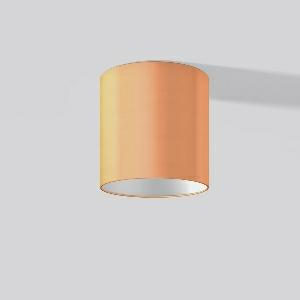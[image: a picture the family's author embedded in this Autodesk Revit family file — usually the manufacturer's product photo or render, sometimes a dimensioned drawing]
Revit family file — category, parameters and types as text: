
# Revit family: toledo_flatliner_901634_002_1_be23
name_source: partatom
category: Lighting Fixtures
units: mm (PartAtom-declared; Revit-internal decimal feet)

## family parameters
Cut with Voids When Loaded = No
Host = Face
Light Source = No
Part Type = Normal
Room Calculation Point = No
Round Connector Dimension = Use Diameter
Shared = No

## types (1)
- 982302.002 (1 x LED Modul 840, 1950 lm, 4000)
    Apparent Load = 22 VA
    CIE Flux Codes = 50 82 97 99 100
    Color Rendering = 80
    Color Temperature = 4000
    Default Elevation = 1800 mm
    Description = Series: TOLEDO FLATLINER
Decorative ceiling luminaire for interior decoration. Base luminaire prepared for the installation of fabric lampshade. Cylinder housing sheet steel, powder-coated. Housing: die cast aluminium and sheet steel, powder-coated. Bezel ring: die-cast aluminium, powder-coated. Lightguide and diffuser made of non-yellowing plastic (PMMA) opal matt. Modular design: With the basic luminaire, a square or cylindrical fabric lampshade must always be ordered separately. Fabric lampshades can be fitted to the basic luminaire without tools. Order satin finish diffuser as separate accessory. 
Colour: white
Diameter: 330 mm
Height: 70 mm
Lamp: LED
Socket: without socket
Colour temperature: 4000K
Colour rendering index (CRI): 80
System power: 22 W
Rated luminous flux: 1950 lm
Luminous efficiency: 89 lm/W
Control gear: Regulated power supply
Protection class: II
Type of protection: IP 40
    Height = 70 mm
    Lamp = 1 x LED Modul 840
    Lamp Light Flux = 1950 lm
    Lamp count = 1
    Length = 330 mm
    Lifetime = 50000 h
    Luminous efficacy = 89 lm/W
    Manufacturer = RZB
    ModVariant = No
    Model = 901634.002.1
    Mounting Place = Ceiling
    Mounting Type = Surface mounted
    Number of Poles = 1
    OnlyDefault = Yes
    Power Factor = 1
    Product Name = TOLEDO FLATLINER
    Product group = Surface mounted ceiling Fabric lampshade luminaires
    ProductGroupID = 313
    Protection Class = Protection class II
    Protection Degree = IP 40
    RLX_Detail_Level = 1
    RLX_Emergency_Light_Flux = 0 lm
    RLX_Emergency_Type = 0
    RLX_Emergency_Type_DB = No
    RlxData = <blob elided: 63005 chars, md5=0765d0e7>
    Socket = socket
    Standby Power = 0 W
    System Light Flux = 1950 lm
    System Power = 22 W
    Type Image = toledo_flatliner_anbau_rund_orange_odeckel.jpg
    URL = http://relux.com
    VarID = 982302_002_891e
    Voltage = 230 V
    Voltage Range = 220-240 V
    Weight = 0.00 kg
    Width = 0 mm  [stored 0 ft]

note: [stored X ft] marks values corroborated as IEEE doubles in the binary element streams (Revit-internal decimal feet)

## geometry (parser evidence)
native form markers: Blend x4, Sweep x11
no freeform markers — native parametric forms only
